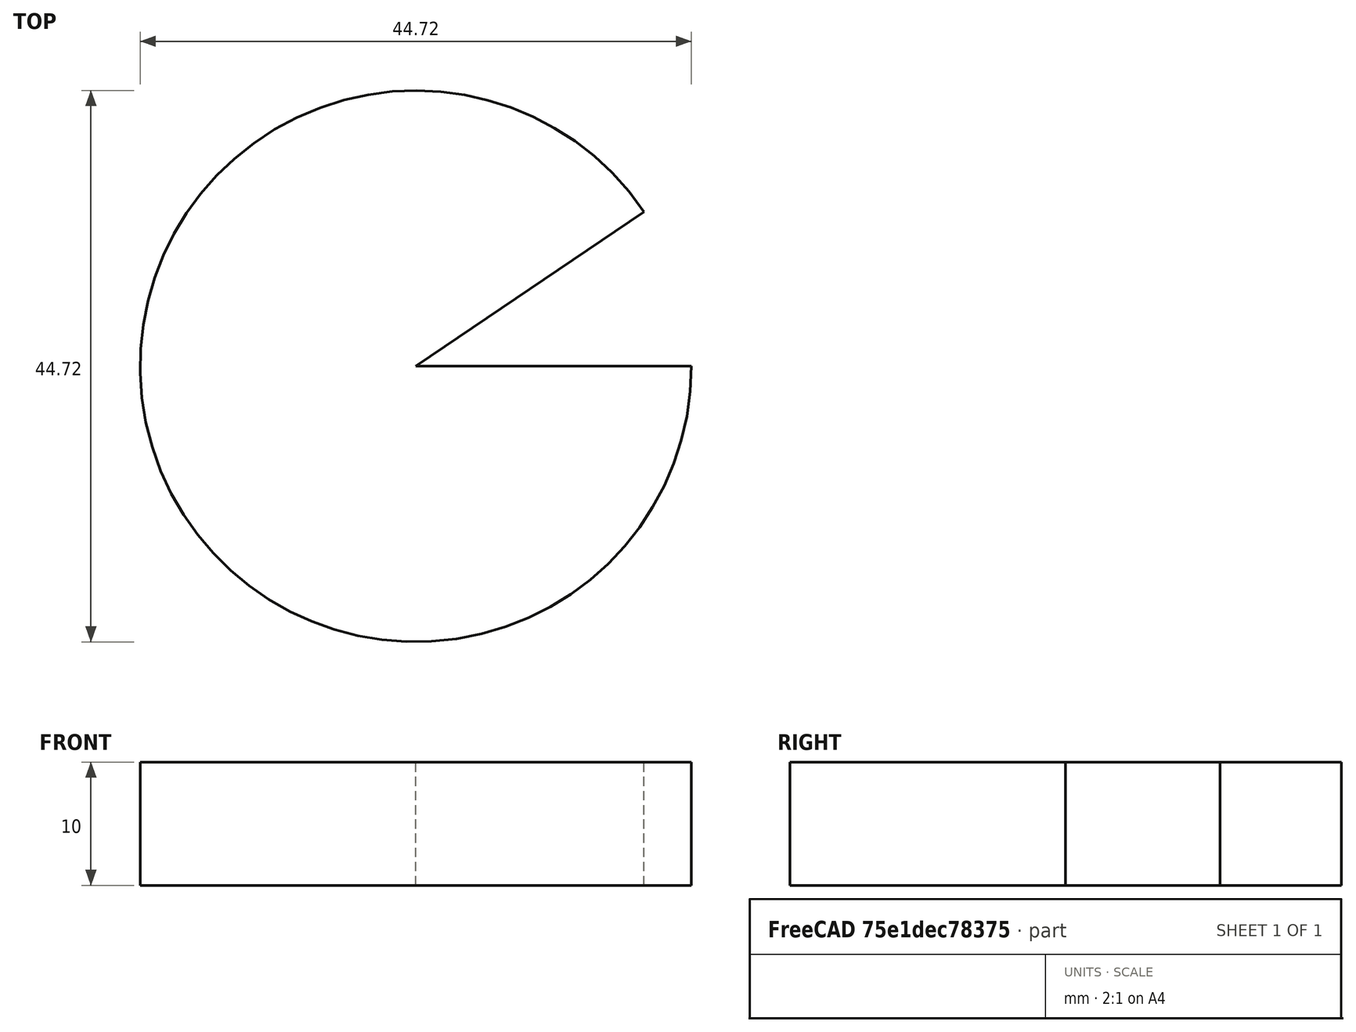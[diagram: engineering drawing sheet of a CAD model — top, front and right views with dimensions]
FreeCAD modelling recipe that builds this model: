
FCSTD DOCUMENT  (FreeCAD 2024.2R37179 (Git))
Label: test
License: All rights reserved
LicenseURL: http://en.wikipedia.org/wiki/All_rights_reserved
objects: Sketcher::SketchObject×1, PartDesign::Pad×1, PartDesign::Body×1
note: 4 computed .brp shape members not serialized (recipe doc carries the construction recipe); baked Part::Feature solids carry a one-line shape summary decoded from their .brp

FEATURE [Sketcher::SketchObject] Sketch
  AttachmentSupport = -> [XY_Plane]
  FullyConstrained = false
  MapMode = 5
  sketch-geometry (3):
    g0: ArcOfCircle CenterX=0 CenterY=-3.29e-14 CenterZ=0 NormalX=0 NormalY=0 NormalZ=1 AngleXU=0 Radius=22.3607 StartAngle=0.594696 EndAngle=6.28319
    g1: LineSegment StartX=0 StartY=-3.29e-14 StartZ=0 EndX=18.5218 EndY=12.5277 EndZ=0
    g2: LineSegment StartX=0 StartY=-3.29e-14 StartZ=0 EndX=22.3607 EndY=-3.29e-14 EndZ=0
  constraints (6):
    c: Coincident(g0,g-1)
    c: Coincident(g1,g0)
    c: Coincident(g2,g0)
    c: Horizontal(g2)
    c: Coincident(g0,g2)
    c: Coincident(g0,g1)
FEATURE [PartDesign::Pad] Pad
  Direction = (0,0,1)
  Length = 10
  Length2 = 10
  Profile = -> Sketch
  ReferenceAxis = -> Sketch [N_Axis]
  Refine = true
  Suppressed = false
  Type = 0
FEATURE [PartDesign::Body] Body  label="Pacman"
  Group = -> [Sketch,Pad]
  Origin = -> Origin
  Tip = -> Pad
